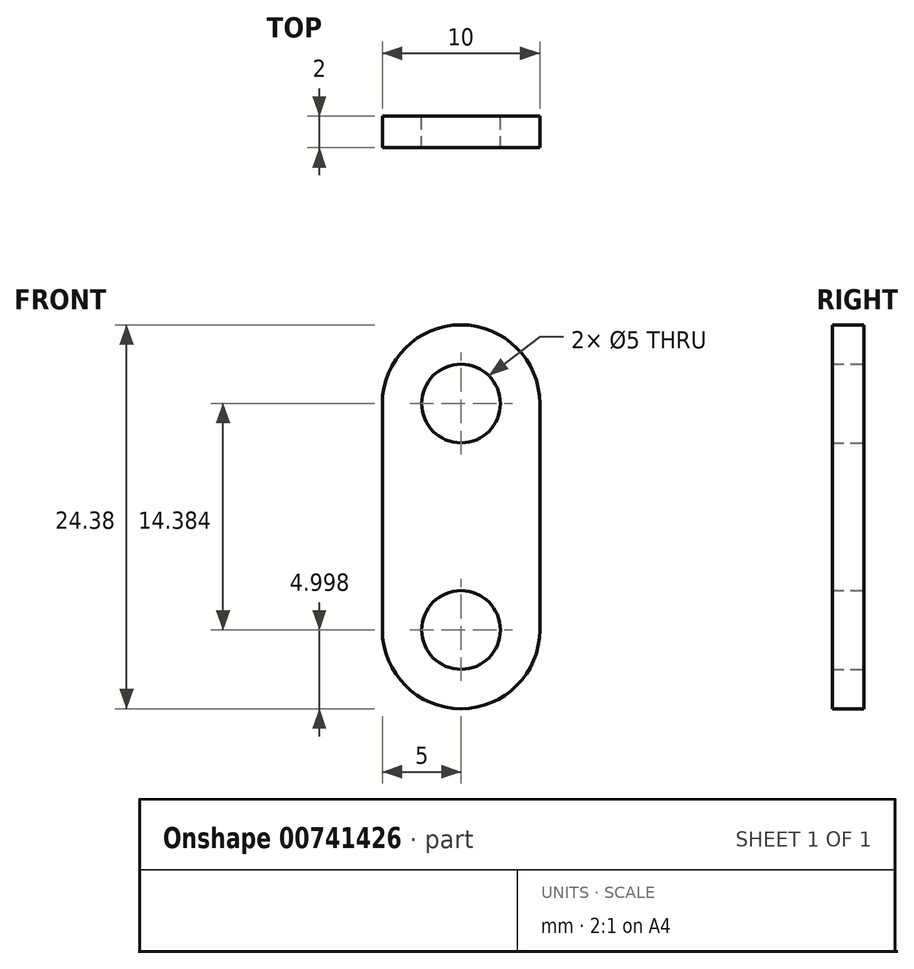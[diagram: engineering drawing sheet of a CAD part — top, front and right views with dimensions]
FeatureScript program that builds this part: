
annotation { "Feature Type Name" : "Feature", "Feature Type Description" : "" }
export const myFeature = defineFeature(function(context is Context, id is Id, definition is map)
    precondition{}
    {
        {
            var Q0;
            Q0=qCreatedBy(makeId("Front.planeOp"),FACE);
            var sketch = newSketch(context, id + "F0", { "sketchPlane" : qUnion([Q0])});
            skCircle(sketch, "E0", {"center": v(0, 5.9) * mm, "radius": 2.5 * mm});
            skArc(sketch, "E1", {"start": v(5, 5.9) * mm, "mid": v(0, 10.9) * mm, "end": v(-5, 5.9) * mm});
            skCircle(sketch, "E2", {"center": v(0, -8.5) * mm, "radius": 2.5 * mm});
            skArc(sketch, "E3", {"start": v(-5, -8.5) * mm, "mid": v(0, -13.5) * mm, "end": v(5, -8.5) * mm});
            skLineSegment(sketch, "E4", {"start": v(-5, 5.9) * mm, "end": v(-5, -8.5) * mm});
            skLineSegment(sketch, "E5", {"start": v(5, 5.9) * mm, "end": v(5, -8.5) * mm});
            skSolve(sketch);
        }
        {
            var Q0;
            Q0 = qSketchRegion(id + "F0", true);
            extrude(context, id + "F1", {"entities" : qUnion([Q0]), "depth" : 2 * mm, "offsetDistance" : 25.4 * mm});
        }
    });
